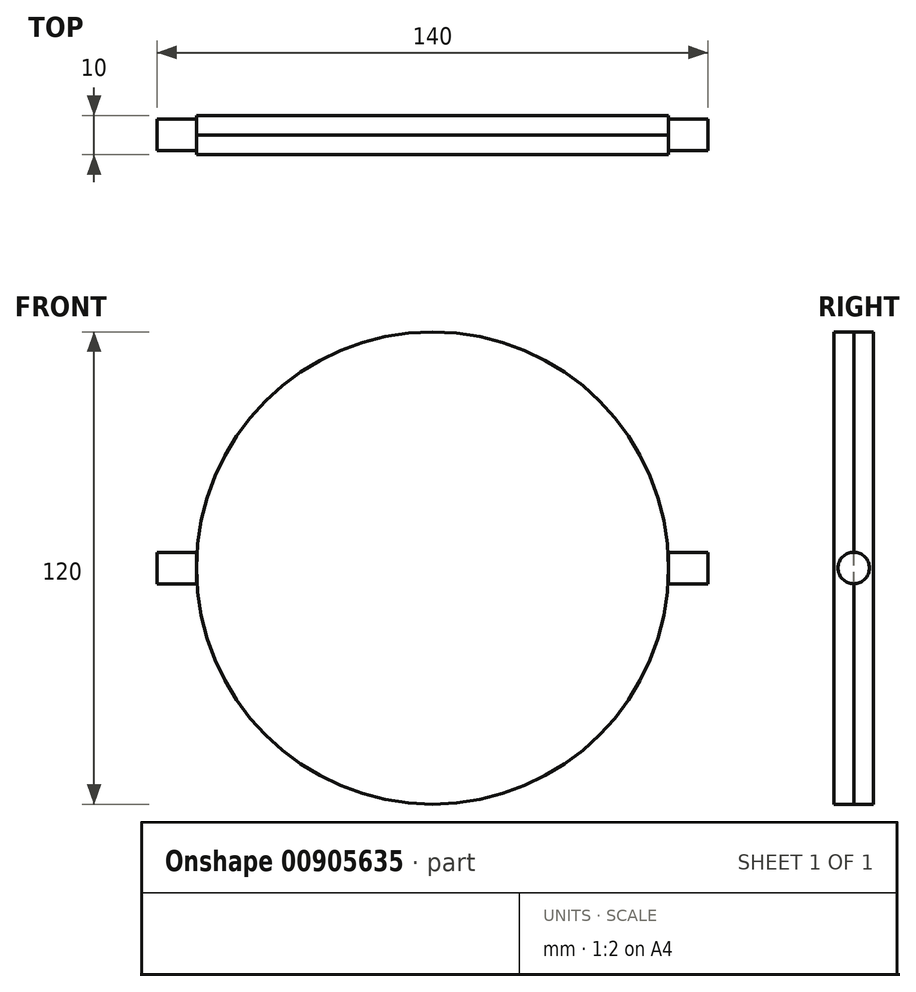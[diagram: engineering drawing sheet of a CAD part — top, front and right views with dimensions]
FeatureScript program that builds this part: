
annotation { "Feature Type Name" : "Feature", "Feature Type Description" : "" }
export const myFeature = defineFeature(function(context is Context, id is Id, definition is map)
    precondition{}
    {
        {
            var Q0;
            Q0=qCreatedBy(makeId("Front.planeOp"),FACE);
            var sketch = newSketch(context, id + "F0", { "sketchPlane" : qUnion([Q0])});
            skCircle(sketch, "E0", {"center": v(0, 0) * mm, "radius": 60 * mm});
            skSolve(sketch);
        }
        {
            var Q0;
            Q0=qCreatedBy(makeId("Front.planeOp"),FACE);
            var sketch = newSketch(context, id + "F1", { "sketchPlane" : qUnion([Q0])});
            skLineSegment(sketch, "E1.bottom", {"start": v(-60, 0) * mm, "end": v(-70, 0) * mm});
            skLineSegment(sketch, "E1.top", {"start": v(-60, 4) * mm, "end": v(-70, 4) * mm});
            skLineSegment(sketch, "E1.left", {"start": v(-60, 0) * mm, "end": v(-60, 4) * mm});
            skLineSegment(sketch, "E1.right", {"start": v(-70, 0) * mm, "end": v(-70, 4) * mm});
            skSolve(sketch);
        }
        {
            var Q0;
            Q0=qCreatedBy(makeId("Front.planeOp"),FACE);
            var sketch = newSketch(context, id + "F2", { "sketchPlane" : qUnion([Q0])});
            skLineSegment(sketch, "E2.bottom", {"start": v(60, 0) * mm, "end": v(70, 0) * mm});
            skLineSegment(sketch, "E2.top", {"start": v(60, 4) * mm, "end": v(70, 4) * mm});
            skLineSegment(sketch, "E2.left", {"start": v(60, 0) * mm, "end": v(60, 4) * mm});
            skLineSegment(sketch, "E2.right", {"start": v(70, 0) * mm, "end": v(70, 4) * mm});
            skSolve(sketch);
        }
        {
            var Q0;
            Q0=makeQuery(id+"F1.imprint","IMPRINT",FACE,{"disambiguationData":[TD([[makeQuery(id+"F1.imprint","IMPRINT",EDGE,{"derivedFrom":sQuery(id+"F1.wireOp",EDGE,"E1.bottom")}),-1.0]])]});
            var Q1;
            Q1=sQuery(id+"F1.wireOp",EDGE,"E1.bottom");
            revolve(context, id + "F3", {"surfaceOperationType" : NewSurfaceOperationType.NEW, "entities" : qUnion([Q0]), "axis" : qUnion([Q1]), "revolveType" : RevolveType.FULL});
        }
        {
            var Q0;
            Q0=makeQuery(id+"F2.imprint","IMPRINT",FACE,{"disambiguationData":[TD([[makeQuery(id+"F2.imprint","IMPRINT",EDGE,{"derivedFrom":sQuery(id+"F2.wireOp",EDGE,"E2.bottom")}),1.0]])]});
            var Q1;
            Q1=sQuery(id+"F2.wireOp",EDGE,"E2.bottom");
            revolve(context, id + "F4", {"surfaceOperationType" : NewSurfaceOperationType.NEW, "entities" : qUnion([Q0]), "axis" : qUnion([Q1]), "revolveType" : RevolveType.FULL});
        }
        {
            var Q0;
            Q0=makeQuery(id+"F0.imprint","IMPRINT",FACE,{"disambiguationData":[TD([[makeQuery(id+"F0.imprint","IMPRINT",EDGE,{"derivedFrom":sQuery(id+"F0.wireOp",EDGE,"E0")}),1.0]])]});
            extrude(context, id + "F5", {"entities" : qUnion([Q0]), "depth" : 5 * mm, "offsetDistance" : 25 * mm});
        }
        {
            var Q0;
            Q0=makeQuery(id+"F5.opExtrude","SWEPT_BODY",BODY,{"disambiguationData":[OSD([sQuery(id+"F0.wireOp",EDGE,"E0")])]});
            var Q1;
            Q1=qCreatedBy(makeId("Front.planeOp"),FACE);
            mirror(context, id + "F6", {"entities" : qUnion([Q0]), "mirrorPlane" : qUnion([Q1])});
        }
    });
